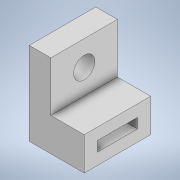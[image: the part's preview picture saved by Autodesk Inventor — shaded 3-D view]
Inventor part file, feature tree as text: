
AUTODESK INVENTOR PART (.ipt)
format: ipt  version: 2020 (Build 240168000, 168)  size: 253,440 bytes
history: native  units: mm
features: extrude x3, sketch x3
ambient origin geometry x8: Origin, YZ Plane, XZ Plane, XY Plane, X Axis, Y Axis, Z Axis, Center Point
bodies: Solid1 (feature_tree)
feature tree (6):
  extrude  "Extrusion1"  Depth=20.0mm
  extrude  "Extrusion2"  Depth=12.0mm
  extrude  "Extrusion3"  Depth=10.0mm
  sketch  "Sketch1"  dims[d0=25.0mm d1=20.0mm]
  sketch  "Sketch2"  dims[d2=3.0mm d3=12.0mm]
  sketch  "Sketch3"  dims[d4=6.5mm d5=0.0mm d6=10.0mm d7=10.0mm d8=0.0mm d9=6.4mm d10=10.0mm d11=0.0mm]
